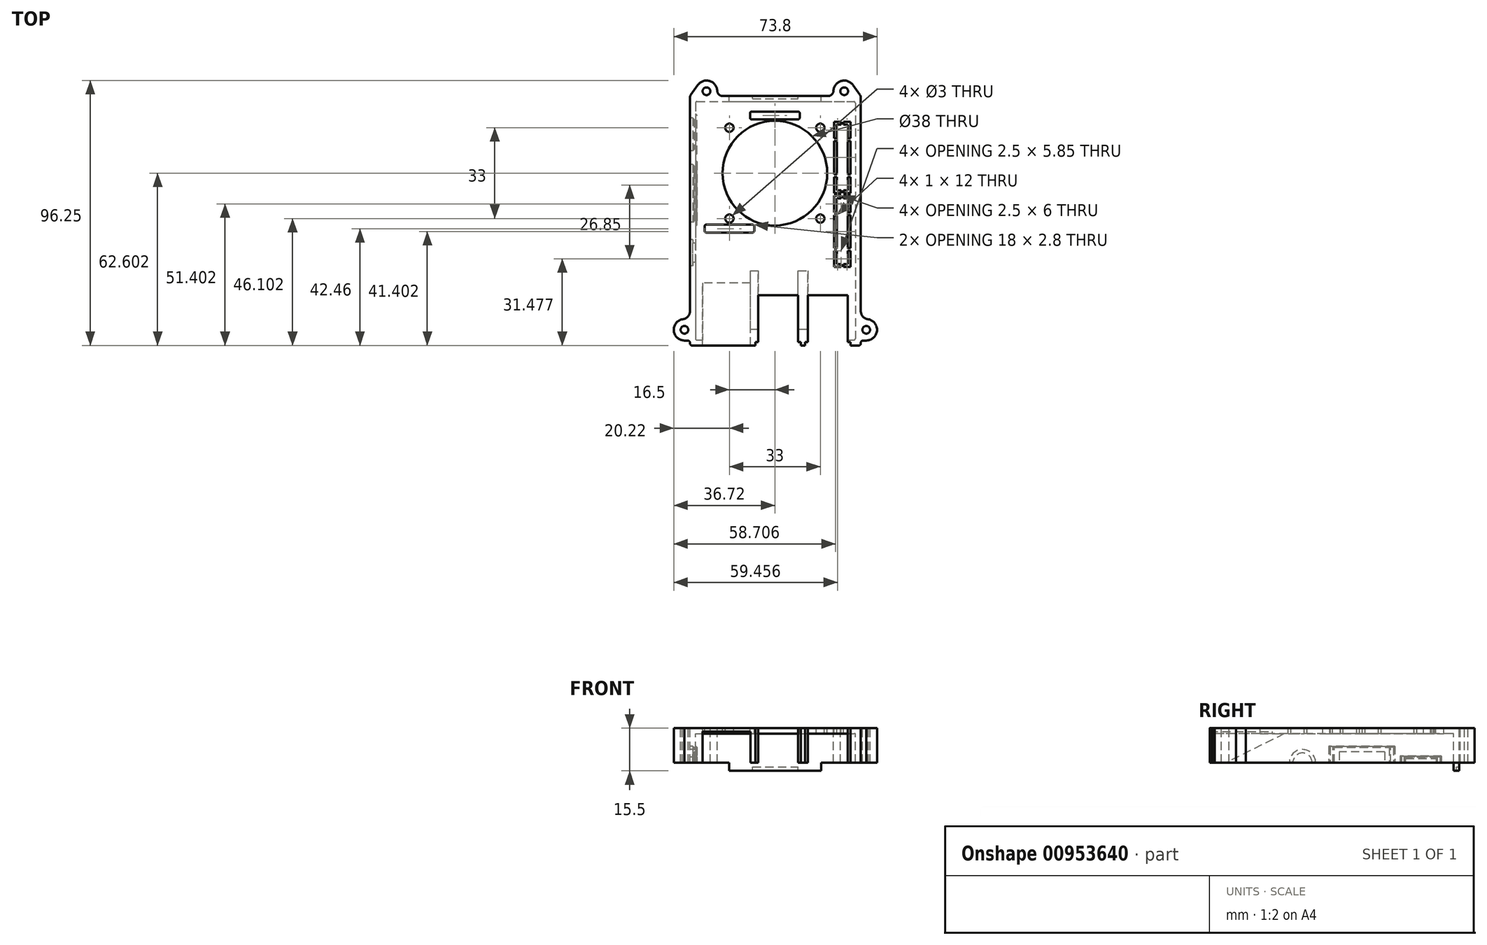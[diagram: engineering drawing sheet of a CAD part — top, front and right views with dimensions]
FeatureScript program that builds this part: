
annotation { "Feature Type Name" : "Feature", "Feature Type Description" : "" }
export const myFeature = defineFeature(function(context is Context, id is Id, definition is map)
    precondition{}
    {
        {
            var Q0;
            Q0=qCreatedBy(makeId("Top.planeOp"),FACE);
            var sketch = newSketch(context, id + "F0", { "sketchPlane" : qUnion([Q0])});
            skLineSegment(sketch, "E0.bottom", {"start": v(-18.95, 42.44) * mm, "end": v(19.3, 42.44) * mm});
            skLineSegment(sketch, "E0.top", {"start": v(-30.81, -48.16) * mm, "end": v(31.19, -48.16) * mm});
            skLineSegment(sketch, "E0.left", {"start": v(-30.81, 42.44) * mm, "end": v(-30.81, -35.67) * mm});
            skLineSegment(sketch, "E0.right", {"start": v(31.19, 42.44) * mm, "end": v(31.19, -35.68) * mm});
            skLineSegment(sketch, "E1.0", {"start": v(-28.31, -46.16) * mm, "end": v(28.69, -46.16) * mm});
            skLineSegment(sketch, "E1.1", {"start": v(29.19, 39.94) * mm, "end": v(29.19, -45.66) * mm});
            skLineSegment(sketch, "E1.2", {"start": v(-28.31, 40.44) * mm, "end": v(28.69, 40.44) * mm});
            skLineSegment(sketch, "E2.0", {"start": v(-28.81, 39.94) * mm, "end": v(-28.81, -45.66) * mm});
            skPoint(sketch, "E3.visualSharp", {"position": v(-28.81, 40.44) * mm});
            skArc(sketch, "E3.filletArc", {"start": v(-28.31, 40.44) * mm, "mid": v(-28.67, 40.3) * mm, "end": v(-28.81, 39.94) * mm});
            skPoint(sketch, "E4.visualSharp", {"position": v(29.19, 40.44) * mm});
            skArc(sketch, "E4.filletArc", {"start": v(29.19, 39.94) * mm, "mid": v(29.04, 40.3) * mm, "end": v(28.69, 40.44) * mm});
            skPoint(sketch, "E5.visualSharp", {"position": v(-28.81, -46.16) * mm});
            skArc(sketch, "E5.filletArc", {"start": v(-28.81, -45.66) * mm, "mid": v(-28.67, -46.01) * mm, "end": v(-28.31, -46.16) * mm});
            skPoint(sketch, "E6.visualSharp", {"position": v(29.19, -46.16) * mm});
            skArc(sketch, "E6.filletArc", {"start": v(28.69, -46.16) * mm, "mid": v(29.04, -46.01) * mm, "end": v(29.19, -45.66) * mm});
            skCircle(sketch, "E7", {"center": v(-24.82, 44.19) * mm, "radius": 1.4 * mm});
            skArc(sketch, "E8", {"start": v(-20.92, 44.35) * mm, "mid": v(-23.72, 47.93) * mm, "end": v(-28, 46.43) * mm});
            skLineSegment(sketch, "E9", {"start": v(-30.81, 42.44) * mm, "end": v(-28, 46.43) * mm});
            skFitSpline(sketch, "E10", {"points": [v(-18.95, 42.44) * mm, v(-20.92, 44.35) * mm], "startDerivative": vector(-2.9, 0) * mm, "endDerivative": vector(-0.3, 3.45) * mm});
            skFitSpline(sketch, "E11.MirrorCS", {"points": [v(19.3, 42.44) * mm, v(21.27, 44.35) * mm], "startDerivative": vector(2.9, 0) * mm, "endDerivative": vector(0.3, 3.45) * mm});
            skArc(sketch, "E12.MirrorCS", {"start": v(21.27, 44.35) * mm, "mid": v(24.07, 47.93) * mm, "end": v(28.36, 46.43) * mm});
            skLineSegment(sketch, "E13.MirrorCS", {"start": v(31.19, 42.44) * mm, "end": v(28.36, 46.43) * mm});
            skCircle(sketch, "E14.MirrorC", {"center": v(25.17, 44.19) * mm, "radius": 1.4 * mm});
            skCircle(sketch, "E15", {"center": v(-32.82, -42.46) * mm, "radius": 1.4 * mm});
            skArc(sketch, "E16", {"start": v(-33.56, -38.63) * mm, "mid": v(-36.7, -42.84) * mm, "end": v(-32.8, -46.36) * mm});
            skFitSpline(sketch, "E17", {"points": [v(-30.81, -35) * mm, v(-33.56, -38.63) * mm], "startDerivative": vector(0.46, -7.1) * mm, "endDerivative": vector(-4.36, -0.55) * mm});
            skFitSpline(sketch, "E18", {"points": [v(-30.81, -47.43) * mm, v(-32.8, -46.36) * mm], "startDerivative": vector(-0.12, 3.4) * mm, "endDerivative": vector(-4.35, -0.1) * mm});
            skLineSegment(sketch, "E19.trimOffspring", {"start": v(-30.81, -47.43) * mm, "end": v(-30.81, -48.16) * mm});
            skCircle(sketch, "E20.MirrorC", {"center": v(33.18, -42.46) * mm, "radius": 1.4 * mm});
            skFitSpline(sketch, "E21.MirrorCS", {"points": [v(31.17, -47.43) * mm, v(33.15, -46.36) * mm], "startDerivative": vector(0.12, 3.4) * mm, "endDerivative": vector(4.35, -0.1) * mm});
            skArc(sketch, "E22.MirrorCS", {"start": v(33.91, -38.63) * mm, "mid": v(37.06, -42.84) * mm, "end": v(33.15, -46.36) * mm});
            skFitSpline(sketch, "E23.MirrorCS", {"points": [v(31.19, -35) * mm, v(33.91, -38.63) * mm], "startDerivative": vector(-0.46, -7.1) * mm, "endDerivative": vector(4.36, -0.55) * mm});
            skLineSegment(sketch, "E24.trimOffspring", {"start": v(31.19, -47.17) * mm, "end": v(31.19, -48.16) * mm});
            skSolve(sketch);
        }
        {
            var Q0;
            Q0=makeQuery(id+"F0.imprint","IMPRINT",FACE,{"disambiguationData":[TD([[makeQuery(id+"F0.imprint","IMPRINT",EDGE,{"derivedFrom":sQuery(id+"F0.wireOp",EDGE,"E1.0")}),1.0]])]});
            var Q1;
            Q1=makeQuery(id+"F0.imprint","IMPRINT",FACE,{"disambiguationData":[TD([[makeQuery(id+"F0.imprint","IMPRINT",EDGE,{"derivedFrom":sQuery(id+"F0.wireOp",EDGE,"E0.top")}),1.0]])]});
            var Q2;
            {var subQ0=sQuery(id+"F0.wireOp",EDGE,"E11.MirrorCS");Q2=makeQuery(id+"F0.imprint","IMPRINT",FACE,{"disambiguationData":[TD([[makeQuery(id+"F0.imprint","IMPRINT",EDGE,{"derivedFrom":subQ0}),-1.0]])]});}
            extrude(context, id + "F1", {"entities" : qUnion([Q0, Q1, Q2]), "oppositeDirection" : true, "depth" : 2 * mm, "offsetDistance" : 25 * mm});
        }
        {
            var Q0;
            Q0=makeQuery(id+"F0.imprint","IMPRINT",FACE,{"disambiguationData":[TD([[makeQuery(id+"F0.imprint","IMPRINT",EDGE,{"derivedFrom":sQuery(id+"F0.wireOp",EDGE,"E0.bottom")}),-1.0]])]});
            extrude(context, id + "F2", {"entities" : qUnion([Q0]), "operationType" : NewBodyOperationType.ADD, "oppositeDirection" : true, "depth" : 12.5 * mm, "offsetDistance" : 25 * mm});
        }
        {
            var Q0;
            {var subQ0=sQuery(id+"F0.wireOp",EDGE,"E9");var subQ1=sQuery(id+"F0.wireOp",EDGE,"E0.left");Q0=makeQuery(id+"F2.boolean.opBoolean","MERGE",EDGE,{"derivedFrom":[makeQuery(id+"F1.opExtrude","SWEPT_EDGE",EDGE,{"disambiguationData":[OSD([subQ1,subQ0])]}),makeQuery(id+"F2.opExtrude","SWEPT_EDGE",EDGE,{"disambiguationData":[OSD([subQ1,subQ0])]})]});}
            var Q1;
            {var subQ0=sQuery(id+"F0.wireOp",EDGE,"E13.MirrorCS");var subQ1=sQuery(id+"F0.wireOp",EDGE,"E0.right");Q1=makeQuery(id+"F2.boolean.opBoolean","MERGE",EDGE,{"derivedFrom":[makeQuery(id+"F1.opExtrude","SWEPT_EDGE",EDGE,{"disambiguationData":[OSD([subQ1,subQ0])]}),makeQuery(id+"F2.opExtrude","SWEPT_EDGE",EDGE,{"disambiguationData":[OSD([subQ1,subQ0])]})]});}
            fillet(context, id + "F3", {"entities" : qUnion([Q0, Q1]), "radius" : 1.5 * mm, "tangentPropagation" : true, "allowEdgeOverflow" : false});
        }
        {
            var Q0;
            {var subQ0=sQuery(id+"F0.wireOp",EDGE,"E19.trimOffspring");var subQ1=sQuery(id+"F0.wireOp",EDGE,"E0.top");Q0=makeQuery(id+"F2.boolean.opBoolean","MERGE",EDGE,{"derivedFrom":[makeQuery(id+"F1.opExtrude","SWEPT_EDGE",EDGE,{"disambiguationData":[OSD([subQ1,subQ0])]}),makeQuery(id+"F2.opExtrude","SWEPT_EDGE",EDGE,{"disambiguationData":[OSD([subQ1,subQ0])]})]});}
            var Q1;
            {var subQ0=sQuery(id+"F0.wireOp",EDGE,"E24.trimOffspring");var subQ1=sQuery(id+"F0.wireOp",EDGE,"E0.top");Q1=makeQuery(id+"F2.boolean.opBoolean","MERGE",EDGE,{"derivedFrom":[makeQuery(id+"F1.opExtrude","SWEPT_EDGE",EDGE,{"disambiguationData":[OSD([subQ1,subQ0])]}),makeQuery(id+"F2.opExtrude","SWEPT_EDGE",EDGE,{"disambiguationData":[OSD([subQ1,subQ0])]})]});}
            fillet(context, id + "F4", {"entities" : qUnion([Q0, Q1]), "radius" : 0.77 * mm, "tangentPropagation" : true, "allowEdgeOverflow" : false});
        }
        {
            var Q0;
            Q0=makeQuery(id+"F1.opExtrude","CAP_FACE",FACE,{"disambiguationData":[OSD([sQuery(id+"F0.wireOp",EDGE,"E0.bottom"),sQuery(id+"F0.wireOp",EDGE,"E0.top"),sQuery(id+"F0.wireOp",EDGE,"E0.left"),sQuery(id+"F0.wireOp",EDGE,"E0.right"),sQuery(id+"F0.wireOp",EDGE,"E7"),sQuery(id+"F0.wireOp",EDGE,"E8"),sQuery(id+"F0.wireOp",EDGE,"E9"),sQuery(id+"F0.wireOp",EDGE,"E10"),sQuery(id+"F0.wireOp",EDGE,"E11.MirrorCS"),sQuery(id+"F0.wireOp",EDGE,"E12.MirrorCS"),sQuery(id+"F0.wireOp",EDGE,"E13.MirrorCS"),sQuery(id+"F0.wireOp",EDGE,"E14.MirrorC"),sQuery(id+"F0.wireOp",EDGE,"E15"),sQuery(id+"F0.wireOp",EDGE,"E16"),sQuery(id+"F0.wireOp",EDGE,"E17"),sQuery(id+"F0.wireOp",EDGE,"E18"),sQuery(id+"F0.wireOp",EDGE,"E19.trimOffspring"),sQuery(id+"F0.wireOp",EDGE,"E20.MirrorC"),sQuery(id+"F0.wireOp",EDGE,"E21.MirrorCS"),sQuery(id+"F0.wireOp",EDGE,"E22.MirrorCS"),sQuery(id+"F0.wireOp",EDGE,"E23.MirrorCS"),sQuery(id+"F0.wireOp",EDGE,"E24.trimOffspring")])],"isStart":false});
            var sketch = newSketch(context, id + "F5", { "sketchPlane" : qUnion([Q0])});
            skLineSegment(sketch, "E25.bottom", {"start": v(-8.87, 48.16) * mm, "end": v(-6.07, 48.16) * mm});
            skLineSegment(sketch, "E25.top", {"start": v(-8.87, 21.06) * mm, "end": v(-6.07, 21.06) * mm});
            skLineSegment(sketch, "E25.left", {"start": v(-8.87, 48.16) * mm, "end": v(-8.87, 21.06) * mm});
            skLineSegment(sketch, "E25.right", {"start": v(-6.07, 48.16) * mm, "end": v(-6.07, 21.06) * mm});
            skLineSegment(sketch, "E26.bottom", {"start": v(8.43, 48.16) * mm, "end": v(11.93, 48.16) * mm});
            skLineSegment(sketch, "E26.top", {"start": v(8.43, 21.06) * mm, "end": v(11.93, 21.06) * mm});
            skLineSegment(sketch, "E26.left", {"start": v(8.43, 48.16) * mm, "end": v(8.43, 21.06) * mm});
            skLineSegment(sketch, "E26.right", {"start": v(11.93, 48.16) * mm, "end": v(11.93, 21.06) * mm});
            skSolve(sketch);
        }
        {
            var Q0;
            Q0 = qSketchRegion(id + "F5", true);
            extrude(context, id + "F6", {"entities" : qUnion([Q0]), "operationType" : NewBodyOperationType.ADD, "depth" : 10.5 * mm, "offsetDistance" : 25 * mm});
        }
        {
            var Q0;
            Q0=makeQuery(id+"F6.opExtrude","CAP_EDGE",EDGE,{"disambiguationData":[OSD([sQuery(id+"F5.wireOp",EDGE,"E25.top")])],"isStart":false});
            var Q1;
            Q1=makeQuery(id+"F6.opExtrude","CAP_EDGE",EDGE,{"disambiguationData":[OSD([sQuery(id+"F5.wireOp",EDGE,"E26.top")])],"isStart":false});
            chamfer(context, id + "F7", {"entities" : qUnion([Q0, Q1]), "chamferType" : ChamferType.TWO_OFFSETS, "width1" : 21.1 * mm, "oppositeDirection" : false, "width2" : 10.5 * mm, "tangentPropagation" : true});
        }
        {
            var Q0;
            Q0=makeQuery(id+"F0.imprint","IMPRINT",FACE,{"disambiguationData":[TD([[makeQuery(id+"F0.imprint","IMPRINT",EDGE,{"derivedFrom":sQuery(id+"F0.wireOp",EDGE,"E1.0")}),1.0]])]});
            var sketch = newSketch(context, id + "F8", { "sketchPlane" : qUnion([Q0])});
            skLineSegment(sketch, "E27.bottom", {"start": v(-6.07, -29.86) * mm, "end": v(8.43, -29.86) * mm});
            skLineSegment(sketch, "E27.top", {"start": v(-6.07, -48.16) * mm, "end": v(8.43, -48.16) * mm});
            skLineSegment(sketch, "E27.left", {"start": v(-6.07, -29.86) * mm, "end": v(-6.07, -46.93) * mm});
            skLineSegment(sketch, "E27.right", {"start": v(8.43, -29.86) * mm, "end": v(8.43, -46.93) * mm});
            skLineSegment(sketch, "E28.bottom", {"start": v(11.93, -29.86) * mm, "end": v(26.43, -29.86) * mm});
            skLineSegment(sketch, "E28.top", {"start": v(11.93, -48.16) * mm, "end": v(26.43, -48.16) * mm});
            skLineSegment(sketch, "E28.left", {"start": v(11.93, -29.86) * mm, "end": v(11.93, -46.93) * mm});
            skLineSegment(sketch, "E28.right", {"start": v(26.43, -29.86) * mm, "end": v(26.43, -46.93) * mm});
            skLineSegment(sketch, "E29.bottom", {"start": v(-6.07, -48.16) * mm, "end": v(-7.07, -48.16) * mm});
            skLineSegment(sketch, "E29.top", {"start": v(-6.07, -46.93) * mm, "end": v(-7.07, -46.93) * mm});
            skLineSegment(sketch, "E29.right", {"start": v(-7.07, -48.16) * mm, "end": v(-7.07, -46.93) * mm});
            skLineSegment(sketch, "E30.bottom", {"start": v(8.43, -48.16) * mm, "end": v(9.43, -48.16) * mm});
            skLineSegment(sketch, "E30.top", {"start": v(8.43, -46.93) * mm, "end": v(9.43, -46.93) * mm});
            skLineSegment(sketch, "E30.right", {"start": v(9.43, -48.16) * mm, "end": v(9.43, -46.93) * mm});
            skLineSegment(sketch, "E31.bottom", {"start": v(11.93, -48.16) * mm, "end": v(10.93, -48.16) * mm});
            skLineSegment(sketch, "E31.top", {"start": v(11.93, -46.93) * mm, "end": v(10.93, -46.93) * mm});
            skLineSegment(sketch, "E31.right", {"start": v(10.93, -48.16) * mm, "end": v(10.93, -46.93) * mm});
            skLineSegment(sketch, "E32.bottom", {"start": v(26.43, -48.16) * mm, "end": v(27.43, -48.16) * mm});
            skLineSegment(sketch, "E32.top", {"start": v(26.43, -46.93) * mm, "end": v(27.43, -46.93) * mm});
            skLineSegment(sketch, "E32.right", {"start": v(27.43, -48.16) * mm, "end": v(27.43, -46.93) * mm});
            skSolve(sketch);
        }
        {
            var Q0;
            Q0=makeQuery(id+"F8.imprint","IMPRINT",FACE,{"disambiguationData":[TD([[makeQuery(id+"F8.imprint","IMPRINT",EDGE,{"derivedFrom":sQuery(id+"F8.wireOp",EDGE,"E27.top")}),1.0]])]});
            var Q1;
            {var subQ0=sQuery(id+"F8.wireOp",EDGE,"E27.bottom");Q1=makeQuery(id+"F8.imprint","IMPRINT",FACE,{"disambiguationData":[TD([[makeQuery(id+"F8.imprint","IMPRINT",EDGE,{"derivedFrom":subQ0}),-1.0]])]});}
            var Q2;
            Q2=makeQuery(id+"F8.imprint","IMPRINT",FACE,{"disambiguationData":[TD([[makeQuery(id+"F8.imprint","IMPRINT",EDGE,{"derivedFrom":sQuery(id+"F8.wireOp",EDGE,"E28.top")}),1.0]])]});
            var Q3;
            {var subQ0=sQuery(id+"F8.wireOp",EDGE,"E28.bottom");Q3=makeQuery(id+"F8.imprint","IMPRINT",FACE,{"disambiguationData":[TD([[makeQuery(id+"F8.imprint","IMPRINT",EDGE,{"derivedFrom":subQ0}),-1.0]])]});}
            var Q4;
            Q4=makeQuery(id+"F6.boolean.opBoolean","MERGE",FACE,{"derivedFrom":[makeQuery(id+"F2.opExtrude","CAP_FACE",FACE,{"disambiguationData":[OSD([sQuery(id+"F0.wireOp",EDGE,"E0.bottom"),sQuery(id+"F0.wireOp",EDGE,"E0.top"),sQuery(id+"F0.wireOp",EDGE,"E0.left"),sQuery(id+"F0.wireOp",EDGE,"E0.right"),sQuery(id+"F0.wireOp",EDGE,"E1.0"),sQuery(id+"F0.wireOp",EDGE,"E1.1"),sQuery(id+"F0.wireOp",EDGE,"E1.2"),sQuery(id+"F0.wireOp",EDGE,"E2.0"),sQuery(id+"F0.wireOp",EDGE,"E3.filletArc"),sQuery(id+"F0.wireOp",EDGE,"E4.filletArc"),sQuery(id+"F0.wireOp",EDGE,"E5.filletArc"),sQuery(id+"F0.wireOp",EDGE,"E6.filletArc"),sQuery(id+"F0.wireOp",EDGE,"E7"),sQuery(id+"F0.wireOp",EDGE,"E8"),sQuery(id+"F0.wireOp",EDGE,"E9"),sQuery(id+"F0.wireOp",EDGE,"E10"),sQuery(id+"F0.wireOp",EDGE,"E11.MirrorCS"),sQuery(id+"F0.wireOp",EDGE,"E12.MirrorCS"),sQuery(id+"F0.wireOp",EDGE,"E13.MirrorCS"),sQuery(id+"F0.wireOp",EDGE,"E14.MirrorC"),sQuery(id+"F0.wireOp",EDGE,"E15"),sQuery(id+"F0.wireOp",EDGE,"E16"),sQuery(id+"F0.wireOp",EDGE,"E17"),sQuery(id+"F0.wireOp",EDGE,"E18"),sQuery(id+"F0.wireOp",EDGE,"E19.trimOffspring"),sQuery(id+"F0.wireOp",EDGE,"E20.MirrorC"),sQuery(id+"F0.wireOp",EDGE,"E21.MirrorCS"),sQuery(id+"F0.wireOp",EDGE,"E22.MirrorCS"),sQuery(id+"F0.wireOp",EDGE,"E23.MirrorCS"),sQuery(id+"F0.wireOp",EDGE,"E24.trimOffspring")])],"isStart":false}),makeQuery(id+"F6.opExtrude","CAP_FACE",FACE,{"disambiguationData":[OSD([sQuery(id+"F5.wireOp",EDGE,"E25.bottom"),sQuery(id+"F5.wireOp",EDGE,"E25.top"),sQuery(id+"F5.wireOp",EDGE,"E25.left"),sQuery(id+"F5.wireOp",EDGE,"E25.right")])],"isStart":false}),makeQuery(id+"F6.opExtrude","CAP_FACE",FACE,{"disambiguationData":[OSD([sQuery(id+"F5.wireOp",EDGE,"E26.bottom"),sQuery(id+"F5.wireOp",EDGE,"E26.top"),sQuery(id+"F5.wireOp",EDGE,"E26.left"),sQuery(id+"F5.wireOp",EDGE,"E26.right")])],"isStart":false})]});
            extrude(context, id + "F9", {"entities" : qUnion([Q0, Q1, Q2, Q3]), "operationType" : NewBodyOperationType.REMOVE, "endBound" : BoundingType.UP_TO_SURFACE, "oppositeDirection" : true, "depth" : 10.5 * mm, "endBoundEntityFace" : qUnion([Q4]), "offsetDistance" : 25 * mm});
        }
        {
            var Q0;
            Q0=makeQuery(id+"F1.opExtrude","CAP_FACE",FACE,{"disambiguationData":[OSD([sQuery(id+"F0.wireOp",EDGE,"E0.bottom"),sQuery(id+"F0.wireOp",EDGE,"E0.top"),sQuery(id+"F0.wireOp",EDGE,"E0.left"),sQuery(id+"F0.wireOp",EDGE,"E0.right"),sQuery(id+"F0.wireOp",EDGE,"E7"),sQuery(id+"F0.wireOp",EDGE,"E8"),sQuery(id+"F0.wireOp",EDGE,"E9"),sQuery(id+"F0.wireOp",EDGE,"E10"),sQuery(id+"F0.wireOp",EDGE,"E11.MirrorCS"),sQuery(id+"F0.wireOp",EDGE,"E12.MirrorCS"),sQuery(id+"F0.wireOp",EDGE,"E13.MirrorCS"),sQuery(id+"F0.wireOp",EDGE,"E14.MirrorC"),sQuery(id+"F0.wireOp",EDGE,"E15"),sQuery(id+"F0.wireOp",EDGE,"E16"),sQuery(id+"F0.wireOp",EDGE,"E17"),sQuery(id+"F0.wireOp",EDGE,"E18"),sQuery(id+"F0.wireOp",EDGE,"E19.trimOffspring"),sQuery(id+"F0.wireOp",EDGE,"E20.MirrorC"),sQuery(id+"F0.wireOp",EDGE,"E21.MirrorCS"),sQuery(id+"F0.wireOp",EDGE,"E22.MirrorCS"),sQuery(id+"F0.wireOp",EDGE,"E23.MirrorCS"),sQuery(id+"F0.wireOp",EDGE,"E24.trimOffspring")])],"isStart":false});
            var sketch = newSketch(context, id + "F10", { "sketchPlane" : qUnion([Q0])});
            skLineSegment(sketch, "E33.bottom", {"start": v(-26.27, 48.16) * mm, "end": v(-8.87, 48.16) * mm});
            skLineSegment(sketch, "E33.top", {"start": v(-26.27, 25.46) * mm, "end": v(-8.87, 25.46) * mm});
            skLineSegment(sketch, "E33.left", {"start": v(-26.27, 48.16) * mm, "end": v(-26.27, 25.46) * mm});
            skLineSegment(sketch, "E33.right", {"start": v(-8.87, 48.16) * mm, "end": v(-8.87, 25.46) * mm});
            skSolve(sketch);
        }
        {
            var Q0;
            {var subQ0=sQuery(id+"F10.wireOp",EDGE,"E33.bottom");Q0=makeQuery(id+"F10.imprint","IMPRINT",FACE,{"disambiguationData":[TD([[makeQuery(id+"F10.imprint","IMPRINT",EDGE,{"derivedFrom":subQ0}),-1.0]])]});}
            var Q1;
            {var subQ0=sQuery(id+"F10.wireOp",EDGE,"E33.top");Q1=makeQuery(id+"F10.imprint","IMPRINT",FACE,{"disambiguationData":[TD([[makeQuery(id+"F10.imprint","IMPRINT",EDGE,{"derivedFrom":subQ0}),1.0]])]});}
            var Q2;
            {var subQ0=sQuery(id+"F0.wireOp",EDGE,"E17");var subQ1=sQuery(id+"F0.wireOp",EDGE,"E16");var subQ2=sQuery(id+"F0.wireOp",EDGE,"E14.MirrorC");var subQ3=sQuery(id+"F0.wireOp",EDGE,"E13.MirrorCS");var subQ4=sQuery(id+"F0.wireOp",EDGE,"E12.MirrorCS");var subQ5=sQuery(id+"F0.wireOp",EDGE,"E11.MirrorCS");var subQ6=sQuery(id+"F0.wireOp",EDGE,"E10");var subQ7=sQuery(id+"F0.wireOp",EDGE,"E24.trimOffspring");var subQ8=sQuery(id+"F0.wireOp",EDGE,"E9");var subQ9=sQuery(id+"F0.wireOp",EDGE,"E23.MirrorCS");var subQ10=sQuery(id+"F0.wireOp",EDGE,"E8");var subQ11=sQuery(id+"F0.wireOp",EDGE,"E22.MirrorCS");var subQ12=sQuery(id+"F0.wireOp",EDGE,"E7");var subQ13=sQuery(id+"F0.wireOp",EDGE,"E21.MirrorCS");var subQ14=sQuery(id+"F0.wireOp",EDGE,"E6.filletArc");var subQ15=sQuery(id+"F0.wireOp",EDGE,"E20.MirrorC");var subQ16=sQuery(id+"F0.wireOp",EDGE,"E5.filletArc");var subQ17=sQuery(id+"F0.wireOp",EDGE,"E19.trimOffspring");var subQ18=sQuery(id+"F0.wireOp",EDGE,"E4.filletArc");var subQ19=sQuery(id+"F0.wireOp",EDGE,"E18");var subQ20=sQuery(id+"F0.wireOp",EDGE,"E3.filletArc");var subQ21=sQuery(id+"F0.wireOp",EDGE,"E2.0");var subQ22=sQuery(id+"F0.wireOp",EDGE,"E1.2");var subQ23=sQuery(id+"F0.wireOp",EDGE,"E15");var subQ24=sQuery(id+"F0.wireOp",EDGE,"E1.1");var subQ25=sQuery(id+"F0.wireOp",EDGE,"E1.0");var subQ26=sQuery(id+"F0.wireOp",EDGE,"E0.right");var subQ27=sQuery(id+"F0.wireOp",EDGE,"E0.left");var subQ28=sQuery(id+"F0.wireOp",EDGE,"E0.top");var subQ29=sQuery(id+"F0.wireOp",EDGE,"E0.bottom");var subQ30=sQuery(id+"F5.wireOp",EDGE,"E25.left");var subQ31=sQuery(id+"F5.wireOp",EDGE,"E25.right");var subQ32=sQuery(id+"F5.wireOp",EDGE,"E25.top");Q2=makeQuery(id+"F9.boolean.opBoolean","SPLIT",FACE,{"disambiguationData":[TD([makeQuery(id+"F1.opExtrude","SWEPT_FACE",FACE,{"disambiguationData":[OSD([subQ29])]})])],"derivedFrom":makeQuery(id+"F6.boolean.opBoolean","MERGE",FACE,{"derivedFrom":[makeQuery(id+"F2.opExtrude","CAP_FACE",FACE,{"disambiguationData":[OSD([subQ29,subQ28,subQ27,subQ26,subQ25,subQ24,subQ22,subQ21,subQ20,subQ18,subQ16,subQ14,subQ12,subQ10,subQ8,subQ6,subQ5,subQ4,subQ3,subQ2,subQ23,subQ1,subQ0,subQ19,subQ17,subQ15,subQ13,subQ11,subQ9,subQ7])],"isStart":false}),makeQuery(id+"F6.opExtrude","CAP_FACE",FACE,{"disambiguationData":[OSD([sQuery(id+"F5.wireOp",EDGE,"E25.bottom"),subQ32,subQ30,subQ31])],"isStart":false}),makeQuery(id+"F6.opExtrude","CAP_FACE",FACE,{"disambiguationData":[OSD([sQuery(id+"F5.wireOp",EDGE,"E26.bottom"),sQuery(id+"F5.wireOp",EDGE,"E26.top"),sQuery(id+"F5.wireOp",EDGE,"E26.left"),sQuery(id+"F5.wireOp",EDGE,"E26.right")])],"isStart":false})]})});}
            extrude(context, id + "F11", {"entities" : qUnion([Q0, Q1]), "operationType" : NewBodyOperationType.REMOVE, "oppositeDirection" : true, "depth" : 0.8 * mm, "offsetDistance" : 25 * mm, "hasSecondDirection" : true, "secondDirectionBound" : SecondDirectionBoundingType.UP_TO_SURFACE, "secondDirectionOppositeDirection" : false, "secondDirectionDepth" : 25 * mm, "secondDirectionBoundEntityFace" : qUnion([Q2])});
        }
        {
            var Q0;
            {var subQ0=sQuery(id+"F0.wireOp",EDGE,"E0.left");Q0=makeQuery(id+"F2.boolean.opBoolean","MERGE",FACE,{"derivedFrom":[makeQuery(id+"F1.opExtrude","SWEPT_FACE",FACE,{"disambiguationData":[OSD([subQ0])]}),makeQuery(id+"F2.opExtrude","SWEPT_FACE",FACE,{"disambiguationData":[OSD([subQ0])]})]});}
            var sketch = newSketch(context, id + "F12", { "sketchPlane" : qUnion([Q0])});
            skArc(sketch, "E34", {"start": v(19.2, -12.5) * mm, "mid": v(14.46, -7.76) * mm, "end": v(9.71, -12.5) * mm});
            skSolve(sketch);
        }
        {
            var Q0;
            {var subQ0=sQuery(id+"F12.wireOp",EDGE,"E34");Q0=makeQuery(id+"F12.imprint","IMPRINT",FACE,{"disambiguationData":[TD([[makeQuery(id+"F12.imprint","IMPRINT",EDGE,{"derivedFrom":subQ0}),1.0]])]});}
            extrude(context, id + "F13", {"entities" : qUnion([Q0]), "operationType" : NewBodyOperationType.REMOVE, "oppositeDirection" : true, "depth" : 1 * mm, "offsetDistance" : 25 * mm});
        }
        {
            var Q0;
            Q0=makeQuery(id+"F13.boolean.opBoolean","COPY",FACE,{"derivedFrom":makeQuery(id+"F13.opExtrude","CAP_FACE",FACE,{"disambiguationData":[OSD([sQuery(id+"F0.wireOp",EDGE,"E0.left"),sQuery(id+"F12.wireOp",EDGE,"E34")])],"isStart":false})});
            var sketch = newSketch(context, id + "F14", { "sketchPlane" : qUnion([Q0])});
            skArc(sketch, "E35", {"start": v(17.96, -12.5) * mm, "mid": v(14.46, -9) * mm, "end": v(10.96, -12.5) * mm});
            skSolve(sketch);
        }
        {
            var Q0;
            {var subQ0=sQuery(id+"F14.wireOp",EDGE,"E35");Q0=makeQuery(id+"F14.imprint","IMPRINT",FACE,{"disambiguationData":[TD([[makeQuery(id+"F14.imprint","IMPRINT",EDGE,{"derivedFrom":subQ0}),1.0]])]});}
            var Q1;
            Q1=makeQuery(id+"F2.opExtrude","SWEPT_FACE",FACE,{"disambiguationData":[OSD([sQuery(id+"F0.wireOp",EDGE,"E2.0")])]});
            extrude(context, id + "F15", {"entities" : qUnion([Q0]), "operationType" : NewBodyOperationType.REMOVE, "endBound" : BoundingType.UP_TO_SURFACE, "oppositeDirection" : true, "depth" : 25 * mm, "endBoundEntityFace" : qUnion([Q1]), "offsetDistance" : 25 * mm});
        }
        {
            var Q0;
            {var subQ5=sQuery(id+"F12.wireOp",EDGE,"E34");Q0=makeQuery(id+"F12.imprint","IMPRINT",FACE,{"disambiguationData":[TD([[makeQuery(id+"F12.imprint","IMPRINT",EDGE,{"derivedFrom":subQ5}),-1.0]])]});}
            var sketch = newSketch(context, id + "F16", { "sketchPlane" : qUnion([Q0])});
            skLineSegment(sketch, "E36.bottom", {"start": v(3.41, -12.5) * mm, "end": v(-17.59, -12.5) * mm});
            skLineSegment(sketch, "E36.top", {"start": v(3.41, -6.5) * mm, "end": v(-17.59, -6.5) * mm});
            skLineSegment(sketch, "E36.left", {"start": v(3.41, -12.5) * mm, "end": v(3.41, -6.5) * mm});
            skLineSegment(sketch, "E36.right", {"start": v(-17.59, -12.5) * mm, "end": v(-17.59, -6.5) * mm});
            skSolve(sketch);
        }
        {
            var Q0;
            Q0=makeQuery(id+"F16.imprint","IMPRINT",FACE,{"disambiguationData":[TD([[makeQuery(id+"F16.imprint","IMPRINT",EDGE,{"derivedFrom":sQuery(id+"F16.wireOp",EDGE,"E36.bottom")}),1.0]])]});
            extrude(context, id + "F17", {"entities" : qUnion([Q0]), "operationType" : NewBodyOperationType.REMOVE, "oppositeDirection" : true, "depth" : 1.5 * mm, "offsetDistance" : 25 * mm});
        }
        {
            var Q0;
            {var subQ2=sQuery(id+"F0.wireOp",EDGE,"E14.MirrorC");var subQ4=sQuery(id+"F0.wireOp",EDGE,"E13.MirrorCS");var subQ6=sQuery(id+"F0.wireOp",EDGE,"E12.MirrorCS");var subQ8=sQuery(id+"F0.wireOp",EDGE,"E24.trimOffspring");var subQ9=sQuery(id+"F0.wireOp",EDGE,"E0.top");var subQ11=sQuery(id+"F0.wireOp",EDGE,"E11.MirrorCS");var subQ13=sQuery(id+"F0.wireOp",EDGE,"E10");var subQ16=sQuery(id+"F0.wireOp",EDGE,"E9");var subQ18=sQuery(id+"F0.wireOp",EDGE,"E23.MirrorCS");var subQ20=sQuery(id+"F0.wireOp",EDGE,"E8");var subQ22=sQuery(id+"F0.wireOp",EDGE,"E22.MirrorCS");var subQ24=sQuery(id+"F0.wireOp",EDGE,"E7");var subQ26=sQuery(id+"F0.wireOp",EDGE,"E21.MirrorCS");var subQ28=sQuery(id+"F0.wireOp",EDGE,"E6.filletArc");var subQ30=sQuery(id+"F0.wireOp",EDGE,"E0.right");var subQ32=sQuery(id+"F0.wireOp",EDGE,"E20.MirrorC");var subQ34=sQuery(id+"F0.wireOp",EDGE,"E4.filletArc");var subQ36=sQuery(id+"F0.wireOp",EDGE,"E3.filletArc");var subQ38=sQuery(id+"F0.wireOp",EDGE,"E2.0");var subQ40=sQuery(id+"F0.wireOp",EDGE,"E1.2");var subQ42=sQuery(id+"F0.wireOp",EDGE,"E1.1");var subQ46=sQuery(id+"F0.wireOp",EDGE,"E0.left");var subQ51=sQuery(id+"F0.wireOp",EDGE,"E0.bottom");var subQ63=makeQuery(id+"F1.opExtrude","SWEPT_FACE",FACE,{"disambiguationData":[OSD([subQ51])]});var subQ69=sQuery(id+"F0.wireOp",EDGE,"E1.0");var subQ75=sQuery(id+"F0.wireOp",EDGE,"E17");var subQ77=sQuery(id+"F0.wireOp",EDGE,"E16");var subQ79=sQuery(id+"F0.wireOp",EDGE,"E19.trimOffspring");var subQ81=sQuery(id+"F0.wireOp",EDGE,"E5.filletArc");var subQ83=sQuery(id+"F0.wireOp",EDGE,"E18");var subQ87=sQuery(id+"F0.wireOp",EDGE,"E15");var subQ91=sQuery(id+"F5.wireOp",EDGE,"E25.left");var subQ92=sQuery(id+"F5.wireOp",EDGE,"E25.right");var subQ93=sQuery(id+"F5.wireOp",EDGE,"E25.top");Q0=makeQuery(id+"F15.boolean.opBoolean","SPLIT",FACE,{"disambiguationData":[TD([subQ63])],"derivedFrom":makeQuery(id+"F11.boolean.opBoolean","SPLIT",FACE,{"disambiguationData":[TD([subQ63])],"derivedFrom":makeQuery(id+"F9.boolean.opBoolean","SPLIT",FACE,{"disambiguationData":[TD([subQ63])],"derivedFrom":makeQuery(id+"F6.boolean.opBoolean","MERGE",FACE,{"derivedFrom":[makeQuery(id+"F2.opExtrude","CAP_FACE",FACE,{"disambiguationData":[OSD([subQ51,subQ9,subQ46,subQ30,subQ69,subQ42,subQ40,subQ38,subQ36,subQ34,subQ81,subQ28,subQ24,subQ20,subQ16,subQ13,subQ11,subQ6,subQ4,subQ2,subQ87,subQ77,subQ75,subQ83,subQ79,subQ32,subQ26,subQ22,subQ18,subQ8])],"isStart":false}),makeQuery(id+"F6.opExtrude","CAP_FACE",FACE,{"disambiguationData":[OSD([sQuery(id+"F5.wireOp",EDGE,"E25.bottom"),subQ93,subQ91,subQ92])],"isStart":false}),makeQuery(id+"F6.opExtrude","CAP_FACE",FACE,{"disambiguationData":[OSD([sQuery(id+"F5.wireOp",EDGE,"E26.bottom"),sQuery(id+"F5.wireOp",EDGE,"E26.top"),sQuery(id+"F5.wireOp",EDGE,"E26.left"),sQuery(id+"F5.wireOp",EDGE,"E26.right")])],"isStart":false})]})})})});}
            var sketch = newSketch(context, id + "F18", { "sketchPlane" : qUnion([Q0])});
            skLineSegment(sketch, "E37.left", {"start": v(-28.81, 4.9) * mm, "end": v(-28.81, -19.1) * mm});
            skLineSegment(sketch, "E37.right", {"start": v(-28.32, 4.4) * mm, "end": v(-28.32, -18.61) * mm});
            skLineSegment(sketch, "E38", {"start": v(-28.81, 4.9) * mm, "end": v(-28.32, 4.4) * mm});
            skLineSegment(sketch, "E39", {"start": v(-28.81, -19.1) * mm, "end": v(-28.32, -18.61) * mm});
            skLineSegment(sketch, "E40.left", {"start": v(-28.81, -21.01) * mm, "end": v(-28.81, -36.01) * mm});
            skLineSegment(sketch, "E40.right", {"start": v(-28.32, -21.5) * mm, "end": v(-28.32, -35.52) * mm});
            skLineSegment(sketch, "E41", {"start": v(-28.81, -21.01) * mm, "end": v(-28.32, -21.5) * mm});
            skLineSegment(sketch, "E42", {"start": v(-28.81, -36.01) * mm, "end": v(-28.32, -35.52) * mm});
            skSolve(sketch);
        }
        {
            var Q0;
            {var subQ0=sQuery(id+"F18.wireOp",EDGE,"E37.right");Q0=makeQuery(id+"F18.imprint","IMPRINT",FACE,{"disambiguationData":[TD([[makeQuery(id+"F18.imprint","IMPRINT",EDGE,{"derivedFrom":subQ0}),-1.0]])]});}
            extrude(context, id + "F19", {"entities" : qUnion([Q0]), "operationType" : NewBodyOperationType.ADD, "oppositeDirection" : true, "depth" : 6 * mm, "offsetDistance" : 25 * mm});
        }
        {
            var Q0;
            Q0 = qSketchRegion(id + "F18", true);
            extrude(context, id + "F20", {"entities" : qUnion([Q0]), "operationType" : NewBodyOperationType.ADD, "oppositeDirection" : true, "depth" : 2.4 * mm, "offsetDistance" : 25 * mm});
        }
        {
            var Q0;
            Q0=makeQuery(id+"F20.opExtrude","CAP_EDGE",EDGE,{"disambiguationData":[OSD([sQuery(id+"F18.wireOp",EDGE,"E40.right")])],"isStart":false});
            var Q1;
            Q1=makeQuery(id+"F19.opExtrude","CAP_EDGE",EDGE,{"disambiguationData":[OSD([sQuery(id+"F18.wireOp",EDGE,"E37.right")])],"isStart":false});
            chamfer(context, id + "F21", {"entities" : qUnion([Q0, Q1]), "width" : 0.4 * mm, "tangentPropagation" : true});
        }
        {
            var Q0;
            {var subQ5=sQuery(id+"F12.wireOp",EDGE,"E34");Q0=makeQuery(id+"F12.imprint","IMPRINT",FACE,{"disambiguationData":[TD([[makeQuery(id+"F12.imprint","IMPRINT",EDGE,{"derivedFrom":subQ5}),-1.0]])]});}
            var sketch = newSketch(context, id + "F22", { "sketchPlane" : qUnion([Q0])});
            skLineSegment(sketch, "E43.bottom", {"start": v(-22.52, -12.5) * mm, "end": v(-34.52, -12.5) * mm});
            skLineSegment(sketch, "E43.top", {"start": v(-22.52, -10.5) * mm, "end": v(-34.52, -10.5) * mm});
            skLineSegment(sketch, "E43.left", {"start": v(-22.52, -12.5) * mm, "end": v(-22.52, -10.5) * mm});
            skLineSegment(sketch, "E43.right", {"start": v(-34.52, -12.5) * mm, "end": v(-34.52, -10.5) * mm});
            skLineSegment(sketch, "E44.bottom", {"start": v(-15.37, -8.6) * mm, "end": v(1.13, -8.6) * mm});
            skLineSegment(sketch, "E44.top", {"start": v(-15.37, -12.5) * mm, "end": v(1.13, -12.5) * mm});
            skLineSegment(sketch, "E44.left", {"start": v(-15.37, -8.6) * mm, "end": v(-15.37, -12.5) * mm});
            skLineSegment(sketch, "E44.right", {"start": v(1.13, -8.6) * mm, "end": v(1.13, -12.5) * mm});
            skSolve(sketch);
        }
        {
            var Q0;
            Q0=makeQuery(id+"F22.imprint","IMPRINT",FACE,{"disambiguationData":[TD([[makeQuery(id+"F22.imprint","IMPRINT",EDGE,{"derivedFrom":sQuery(id+"F22.wireOp",EDGE,"E44.bottom")}),-1.0]])]});
            var Q1;
            Q1=makeQuery(id+"F19.opExtrude","SWEPT_FACE",FACE,{"disambiguationData":[OSD([sQuery(id+"F18.wireOp",EDGE,"E37.right")])]});
            extrude(context, id + "F23", {"entities" : qUnion([Q0]), "operationType" : NewBodyOperationType.REMOVE, "endBound" : BoundingType.UP_TO_SURFACE, "oppositeDirection" : true, "depth" : 25 * mm, "endBoundEntityFace" : qUnion([Q1]), "offsetDistance" : 25 * mm});
        }
        {
            var Q0;
            Q0=makeQuery(id+"F22.imprint","IMPRINT",FACE,{"disambiguationData":[TD([[makeQuery(id+"F22.imprint","IMPRINT",EDGE,{"derivedFrom":sQuery(id+"F22.wireOp",EDGE,"E43.bottom")}),1.0]])]});
            extrude(context, id + "F24", {"entities" : qUnion([Q0]), "operationType" : NewBodyOperationType.REMOVE, "oppositeDirection" : true, "depth" : 1.5 * mm, "offsetDistance" : 25 * mm});
        }
        {
            var Q0;
            Q0=makeQuery(id+"F17.boolean.opBoolean","COPY",EDGE,{"derivedFrom":makeQuery(id+"F17.opExtrude","CAP_EDGE",EDGE,{"disambiguationData":[OSD([sQuery(id+"F16.wireOp",EDGE,"E36.right")])],"isStart":false})});
            var Q1;
            Q1=makeQuery(id+"F17.boolean.opBoolean","COPY",EDGE,{"derivedFrom":makeQuery(id+"F17.opExtrude","CAP_EDGE",EDGE,{"disambiguationData":[OSD([sQuery(id+"F16.wireOp",EDGE,"E36.top")])],"isStart":false})});
            var Q2;
            Q2=makeQuery(id+"F17.boolean.opBoolean","COPY",EDGE,{"derivedFrom":makeQuery(id+"F17.opExtrude","CAP_EDGE",EDGE,{"disambiguationData":[OSD([sQuery(id+"F16.wireOp",EDGE,"E36.left")])],"isStart":false})});
            var Q3;
            Q3=makeQuery(id+"F24.boolean.opBoolean","COPY",EDGE,{"derivedFrom":makeQuery(id+"F24.opExtrude","CAP_EDGE",EDGE,{"disambiguationData":[OSD([sQuery(id+"F22.wireOp",EDGE,"E43.right")])],"isStart":false})});
            var Q4;
            Q4=makeQuery(id+"F24.boolean.opBoolean","COPY",EDGE,{"derivedFrom":makeQuery(id+"F24.opExtrude","CAP_EDGE",EDGE,{"disambiguationData":[OSD([sQuery(id+"F22.wireOp",EDGE,"E43.top")])],"isStart":false})});
            var Q5;
            Q5=makeQuery(id+"F24.boolean.opBoolean","COPY",EDGE,{"derivedFrom":makeQuery(id+"F24.opExtrude","CAP_EDGE",EDGE,{"disambiguationData":[OSD([sQuery(id+"F22.wireOp",EDGE,"E43.left")])],"isStart":false})});
            chamfer(context, id + "F25", {"entities" : qUnion([Q0, Q1, Q2, Q3, Q4, Q5]), "width" : 0.5 * mm, "tangentPropagation" : true});
        }
        {
            var Q0;
            Q0=qCreatedBy(makeId("Top.planeOp"),FACE);
            var sketch = newSketch(context, id + "F26", { "sketchPlane" : qUnion([Q0])});
            skLineSegment(sketch, "E45.bottom", {"start": v(-16.65, 40.44) * mm, "end": v(16.85, 40.44) * mm});
            skLineSegment(sketch, "E45.top", {"start": v(-16.65, 42.44) * mm, "end": v(16.85, 42.44) * mm});
            skLineSegment(sketch, "E45.left", {"start": v(-16.65, 40.44) * mm, "end": v(-16.65, 42.44) * mm});
            skLineSegment(sketch, "E45.right", {"start": v(16.85, 40.44) * mm, "end": v(16.85, 42.44) * mm});
            skSolve(sketch);
        }
        {
            var Q0;
            Q0 = qSketchRegion(id + "F26", true);
            extrude(context, id + "F27", {"entities" : qUnion([Q0]), "operationType" : NewBodyOperationType.ADD, "oppositeDirection" : true, "depth" : 15.5 * mm, "offsetDistance" : 25 * mm});
        }
        {
            var Q0;
            {var subQ0=sQuery(id+"F0.wireOp",EDGE,"E0.bottom");Q0=makeQuery(id+"F27.boolean.opBoolean","MERGE",FACE,{"derivedFrom":[makeQuery(id+"F2.boolean.opBoolean","MERGE",FACE,{"derivedFrom":[makeQuery(id+"F1.opExtrude","SWEPT_FACE",FACE,{"disambiguationData":[OSD([subQ0])]}),makeQuery(id+"F2.opExtrude","SWEPT_FACE",FACE,{"disambiguationData":[OSD([subQ0])]})]}),makeQuery(id+"F27.opExtrude","SWEPT_FACE",FACE,{"disambiguationData":[OSD([sQuery(id+"F26.wireOp",EDGE,"E45.top")])]})]});}
            var sketch = newSketch(context, id + "F28", { "sketchPlane" : qUnion([Q0])});
            skLineSegment(sketch, "E46.bottom", {"start": v(8.07, -15.5) * mm, "end": v(-8.43, -15.5) * mm});
            skLineSegment(sketch, "E46.top", {"start": v(8.07, -14) * mm, "end": v(-8.43, -14) * mm});
            skLineSegment(sketch, "E46.left", {"start": v(8.07, -15.5) * mm, "end": v(8.07, -14) * mm});
            skLineSegment(sketch, "E46.right", {"start": v(-8.43, -15.5) * mm, "end": v(-8.43, -14) * mm});
            skSolve(sketch);
        }
        {
            var Q0;
            Q0=makeQuery(id+"F28.imprint","IMPRINT",FACE,{"disambiguationData":[TD([[makeQuery(id+"F28.imprint","IMPRINT",EDGE,{"derivedFrom":sQuery(id+"F28.wireOp",EDGE,"E46.bottom")}),-1.0]])]});
            extrude(context, id + "F29", {"entities" : qUnion([Q0]), "operationType" : NewBodyOperationType.REMOVE, "oppositeDirection" : true, "depth" : 1 * mm, "offsetDistance" : 25 * mm});
        }
        {
            var Q0;
            Q0=makeQuery(id+"F1.opExtrude","CAP_FACE",FACE,{"disambiguationData":[OSD([sQuery(id+"F0.wireOp",EDGE,"E0.bottom"),sQuery(id+"F0.wireOp",EDGE,"E0.top"),sQuery(id+"F0.wireOp",EDGE,"E0.left"),sQuery(id+"F0.wireOp",EDGE,"E0.right"),sQuery(id+"F0.wireOp",EDGE,"E7"),sQuery(id+"F0.wireOp",EDGE,"E8"),sQuery(id+"F0.wireOp",EDGE,"E9"),sQuery(id+"F0.wireOp",EDGE,"E10"),sQuery(id+"F0.wireOp",EDGE,"E11.MirrorCS"),sQuery(id+"F0.wireOp",EDGE,"E12.MirrorCS"),sQuery(id+"F0.wireOp",EDGE,"E13.MirrorCS"),sQuery(id+"F0.wireOp",EDGE,"E14.MirrorC"),sQuery(id+"F0.wireOp",EDGE,"E15"),sQuery(id+"F0.wireOp",EDGE,"E16"),sQuery(id+"F0.wireOp",EDGE,"E17"),sQuery(id+"F0.wireOp",EDGE,"E18"),sQuery(id+"F0.wireOp",EDGE,"E19.trimOffspring"),sQuery(id+"F0.wireOp",EDGE,"E20.MirrorC"),sQuery(id+"F0.wireOp",EDGE,"E21.MirrorCS"),sQuery(id+"F0.wireOp",EDGE,"E22.MirrorCS"),sQuery(id+"F0.wireOp",EDGE,"E23.MirrorCS"),sQuery(id+"F0.wireOp",EDGE,"E24.trimOffspring")])],"isStart":true});
            var sketch = newSketch(context, id + "F30", { "sketchPlane" : qUnion([Q0])});
            skCircle(sketch, "E47", {"center": v(0, 14.44) * mm, "radius": 19 * mm});
            skCircle(sketch, "E48", {"center": v(-16.5, 30.94) * mm, "radius": 1.5 * mm});
            skCircle(sketch, "E49", {"center": v(-16.5, -2.06) * mm, "radius": 1.5 * mm});
            skCircle(sketch, "E50", {"center": v(16.5, 30.94) * mm, "radius": 1.5 * mm});
            skCircle(sketch, "E51", {"center": v(16.5, -2.06) * mm, "radius": 1.5 * mm});
            skSolve(sketch);
        }
        {
            var Q0;
            Q0 = qSketchRegion(id + "F30", true);
            var Q1;
            Q1=makeQuery(id+"F1.opExtrude","CAP_FACE",FACE,{"disambiguationData":[OSD([sQuery(id+"F0.wireOp",EDGE,"E0.bottom"),sQuery(id+"F0.wireOp",EDGE,"E0.top"),sQuery(id+"F0.wireOp",EDGE,"E0.left"),sQuery(id+"F0.wireOp",EDGE,"E0.right"),sQuery(id+"F0.wireOp",EDGE,"E7"),sQuery(id+"F0.wireOp",EDGE,"E8"),sQuery(id+"F0.wireOp",EDGE,"E9"),sQuery(id+"F0.wireOp",EDGE,"E10"),sQuery(id+"F0.wireOp",EDGE,"E11.MirrorCS"),sQuery(id+"F0.wireOp",EDGE,"E12.MirrorCS"),sQuery(id+"F0.wireOp",EDGE,"E13.MirrorCS"),sQuery(id+"F0.wireOp",EDGE,"E14.MirrorC"),sQuery(id+"F0.wireOp",EDGE,"E15"),sQuery(id+"F0.wireOp",EDGE,"E16"),sQuery(id+"F0.wireOp",EDGE,"E17"),sQuery(id+"F0.wireOp",EDGE,"E18"),sQuery(id+"F0.wireOp",EDGE,"E19.trimOffspring"),sQuery(id+"F0.wireOp",EDGE,"E20.MirrorC"),sQuery(id+"F0.wireOp",EDGE,"E21.MirrorCS"),sQuery(id+"F0.wireOp",EDGE,"E22.MirrorCS"),sQuery(id+"F0.wireOp",EDGE,"E23.MirrorCS"),sQuery(id+"F0.wireOp",EDGE,"E24.trimOffspring")])],"isStart":false});
            extrude(context, id + "F31", {"entities" : qUnion([Q0]), "operationType" : NewBodyOperationType.REMOVE, "endBound" : BoundingType.UP_TO_SURFACE, "oppositeDirection" : true, "depth" : 25 * mm, "endBoundEntityFace" : qUnion([Q1]), "offsetDistance" : 25 * mm});
        }
        {
            var Q0;
            Q0=makeQuery(id+"F1.opExtrude","CAP_FACE",FACE,{"disambiguationData":[OSD([sQuery(id+"F0.wireOp",EDGE,"E0.bottom"),sQuery(id+"F0.wireOp",EDGE,"E0.top"),sQuery(id+"F0.wireOp",EDGE,"E0.left"),sQuery(id+"F0.wireOp",EDGE,"E0.right"),sQuery(id+"F0.wireOp",EDGE,"E7"),sQuery(id+"F0.wireOp",EDGE,"E8"),sQuery(id+"F0.wireOp",EDGE,"E9"),sQuery(id+"F0.wireOp",EDGE,"E10"),sQuery(id+"F0.wireOp",EDGE,"E11.MirrorCS"),sQuery(id+"F0.wireOp",EDGE,"E12.MirrorCS"),sQuery(id+"F0.wireOp",EDGE,"E13.MirrorCS"),sQuery(id+"F0.wireOp",EDGE,"E14.MirrorC"),sQuery(id+"F0.wireOp",EDGE,"E15"),sQuery(id+"F0.wireOp",EDGE,"E16"),sQuery(id+"F0.wireOp",EDGE,"E17"),sQuery(id+"F0.wireOp",EDGE,"E18"),sQuery(id+"F0.wireOp",EDGE,"E19.trimOffspring"),sQuery(id+"F0.wireOp",EDGE,"E20.MirrorC"),sQuery(id+"F0.wireOp",EDGE,"E21.MirrorCS"),sQuery(id+"F0.wireOp",EDGE,"E22.MirrorCS"),sQuery(id+"F0.wireOp",EDGE,"E23.MirrorCS"),sQuery(id+"F0.wireOp",EDGE,"E24.trimOffspring")])],"isStart":true});
            var sketch = newSketch(context, id + "F32", { "sketchPlane" : qUnion([Q0])});
            skLineSegment(sketch, "E52.bottom", {"start": v(22.49, 32.1) * mm, "end": v(26.49, 32.1) * mm});
            skLineSegment(sketch, "E52.top", {"start": v(22.49, 8.24) * mm, "end": v(26.49, 8.24) * mm});
            skLineSegment(sketch, "E52.left", {"start": v(22.49, 32.1) * mm, "end": v(22.49, 8.24) * mm});
            skLineSegment(sketch, "E52.right", {"start": v(26.49, 32.1) * mm, "end": v(26.49, 8.24) * mm});
            skLineSegment(sketch, "E53.bottom", {"start": v(22.49, 5.24) * mm, "end": v(26.49, 5.24) * mm});
            skLineSegment(sketch, "E53.top", {"start": v(22.49, -18.6) * mm, "end": v(26.49, -18.6) * mm});
            skLineSegment(sketch, "E53.left", {"start": v(22.49, 5.24) * mm, "end": v(22.49, -18.6) * mm});
            skLineSegment(sketch, "E53.right", {"start": v(26.49, 5.24) * mm, "end": v(26.49, -18.6) * mm});
            skLineSegment(sketch, "E54.0", {"start": v(21.49, 33.1) * mm, "end": v(27.49, 33.1) * mm});
            skLineSegment(sketch, "E54.1", {"start": v(21.49, 33.1) * mm, "end": v(21.49, 7.24) * mm});
            skLineSegment(sketch, "E54.2", {"start": v(21.49, 7.24) * mm, "end": v(27.49, 7.24) * mm});
            skLineSegment(sketch, "E54.3", {"start": v(27.49, 33.1) * mm, "end": v(27.49, 7.24) * mm});
            skLineSegment(sketch, "E55.0", {"start": v(21.49, 6.24) * mm, "end": v(27.49, 6.24) * mm});
            skLineSegment(sketch, "E55.1", {"start": v(21.49, 6.24) * mm, "end": v(21.49, -19.6) * mm});
            skLineSegment(sketch, "E55.2", {"start": v(21.49, -19.6) * mm, "end": v(27.49, -19.6) * mm});
            skLineSegment(sketch, "E55.3", {"start": v(27.49, 6.24) * mm, "end": v(27.49, -19.6) * mm});
            skLineSegment(sketch, "E56", {"start": v(23.99, 33.1) * mm, "end": v(23.99, 32.1) * mm});
            skLineSegment(sketch, "E57", {"start": v(24.99, 33.1) * mm, "end": v(24.99, 32.1) * mm});
            skLineSegment(sketch, "E58", {"start": v(23.99, 8.24) * mm, "end": v(23.99, 7.24) * mm});
            skLineSegment(sketch, "E59", {"start": v(24.99, 8.24) * mm, "end": v(24.99, 7.24) * mm});
            skLineSegment(sketch, "E60", {"start": v(23.99, 6.24) * mm, "end": v(23.99, 5.24) * mm});
            skLineSegment(sketch, "E61", {"start": v(24.99, 6.24) * mm, "end": v(24.99, 5.24) * mm});
            skLineSegment(sketch, "E62", {"start": v(23.99, -18.6) * mm, "end": v(23.99, -19.6) * mm});
            skLineSegment(sketch, "E63", {"start": v(24.99, -18.6) * mm, "end": v(24.99, -19.6) * mm});
            skLineSegment(sketch, "E64", {"start": v(21.49, 0.24) * mm, "end": v(22.49, 0.24) * mm});
            skLineSegment(sketch, "E65", {"start": v(21.49, -0.76) * mm, "end": v(22.49, -0.76) * mm});
            skLineSegment(sketch, "E66", {"start": v(26.49, 0.24) * mm, "end": v(27.49, 0.24) * mm});
            skLineSegment(sketch, "E67", {"start": v(26.49, -0.76) * mm, "end": v(27.49, -0.76) * mm});
            skLineSegment(sketch, "E68", {"start": v(21.49, -12.76) * mm, "end": v(22.49, -12.76) * mm});
            skLineSegment(sketch, "E69", {"start": v(21.49, -13.76) * mm, "end": v(22.49, -13.76) * mm});
            skLineSegment(sketch, "E70", {"start": v(26.49, -12.76) * mm, "end": v(27.49, -12.76) * mm});
            skLineSegment(sketch, "E71", {"start": v(26.49, -13.76) * mm, "end": v(27.49, -13.76) * mm});
            skLineSegment(sketch, "E72", {"start": v(21.49, 27.1) * mm, "end": v(22.49, 27.1) * mm});
            skLineSegment(sketch, "E73", {"start": v(21.49, 26.1) * mm, "end": v(22.49, 26.1) * mm});
            skLineSegment(sketch, "E74", {"start": v(26.49, 27.1) * mm, "end": v(27.49, 27.1) * mm});
            skLineSegment(sketch, "E75", {"start": v(26.49, 26.1) * mm, "end": v(27.49, 26.1) * mm});
            skLineSegment(sketch, "E76", {"start": v(21.49, 14.1) * mm, "end": v(22.49, 14.1) * mm});
            skLineSegment(sketch, "E77", {"start": v(21.49, 13.1) * mm, "end": v(22.49, 13.1) * mm});
            skLineSegment(sketch, "E78", {"start": v(26.49, 14.1) * mm, "end": v(27.49, 14.1) * mm});
            skLineSegment(sketch, "E79", {"start": v(26.49, 13.1) * mm, "end": v(27.49, 13.1) * mm});
            skLineSegment(sketch, "E80.bottom", {"start": v(-9, 36.8) * mm, "end": v(9, 36.8) * mm});
            skLineSegment(sketch, "E80.top", {"start": v(-9, 34) * mm, "end": v(9, 34) * mm});
            skLineSegment(sketch, "E80.left", {"start": v(-9, 36.8) * mm, "end": v(-9, 34) * mm});
            skLineSegment(sketch, "E80.right", {"start": v(9, 36.8) * mm, "end": v(9, 34) * mm});
            skPoint(sketch, "E80.middle", {"position": v(0, 35.4) * mm});
            skLineSegment(sketch, "E81.bottom", {"start": v(-7.5, -4.3) * mm, "end": v(-25.5, -4.3) * mm});
            skLineSegment(sketch, "E81.top", {"start": v(-7.5, -7.1) * mm, "end": v(-25.5, -7.1) * mm});
            skLineSegment(sketch, "E81.left", {"start": v(-7.5, -4.3) * mm, "end": v(-7.5, -7.1) * mm});
            skLineSegment(sketch, "E81.right", {"start": v(-25.5, -4.3) * mm, "end": v(-25.5, -7.1) * mm});
            skPoint(sketch, "E81.middle", {"position": v(-16.5, -5.7) * mm});
            skSolve(sketch);
        }
        {
            var Q0;
            {var subQ3=sQuery(id+"F32.wireOp",EDGE,"E56");Q0=makeQuery(id+"F32.imprint","IMPRINT",FACE,{"disambiguationData":[TD([[makeQuery(id+"F32.imprint","IMPRINT",EDGE,{"derivedFrom":subQ3}),-1.0]])]});}
            var Q1;
            {var subQ4=sQuery(id+"F32.wireOp",EDGE,"E57");Q1=makeQuery(id+"F32.imprint","IMPRINT",FACE,{"disambiguationData":[TD([[makeQuery(id+"F32.imprint","IMPRINT",EDGE,{"derivedFrom":subQ4}),1.0]])]});}
            var Q2;
            {var subQ0=sQuery(id+"F32.wireOp",EDGE,"E73");Q2=makeQuery(id+"F32.imprint","IMPRINT",FACE,{"disambiguationData":[TD([[makeQuery(id+"F32.imprint","IMPRINT",EDGE,{"derivedFrom":subQ0}),-1.0]])]});}
            var Q3;
            {var subQ0=sQuery(id+"F32.wireOp",EDGE,"E75");Q3=makeQuery(id+"F32.imprint","IMPRINT",FACE,{"disambiguationData":[TD([[makeQuery(id+"F32.imprint","IMPRINT",EDGE,{"derivedFrom":subQ0}),-1.0]])]});}
            var Q4;
            {var subQ4=sQuery(id+"F32.wireOp",EDGE,"E58");Q4=makeQuery(id+"F32.imprint","IMPRINT",FACE,{"disambiguationData":[TD([[makeQuery(id+"F32.imprint","IMPRINT",EDGE,{"derivedFrom":subQ4}),-1.0]])]});}
            var Q5;
            {var subQ4=sQuery(id+"F32.wireOp",EDGE,"E59");Q5=makeQuery(id+"F32.imprint","IMPRINT",FACE,{"disambiguationData":[TD([[makeQuery(id+"F32.imprint","IMPRINT",EDGE,{"derivedFrom":subQ4}),1.0]])]});}
            var Q6;
            {var subQ3=sQuery(id+"F32.wireOp",EDGE,"E60");Q6=makeQuery(id+"F32.imprint","IMPRINT",FACE,{"disambiguationData":[TD([[makeQuery(id+"F32.imprint","IMPRINT",EDGE,{"derivedFrom":subQ3}),-1.0]])]});}
            var Q7;
            {var subQ4=sQuery(id+"F32.wireOp",EDGE,"E61");Q7=makeQuery(id+"F32.imprint","IMPRINT",FACE,{"disambiguationData":[TD([[makeQuery(id+"F32.imprint","IMPRINT",EDGE,{"derivedFrom":subQ4}),1.0]])]});}
            var Q8;
            {var subQ0=sQuery(id+"F32.wireOp",EDGE,"E65");Q8=makeQuery(id+"F32.imprint","IMPRINT",FACE,{"disambiguationData":[TD([[makeQuery(id+"F32.imprint","IMPRINT",EDGE,{"derivedFrom":subQ0}),-1.0]])]});}
            var Q9;
            {var subQ0=sQuery(id+"F32.wireOp",EDGE,"E67");Q9=makeQuery(id+"F32.imprint","IMPRINT",FACE,{"disambiguationData":[TD([[makeQuery(id+"F32.imprint","IMPRINT",EDGE,{"derivedFrom":subQ0}),-1.0]])]});}
            var Q10;
            {var subQ4=sQuery(id+"F32.wireOp",EDGE,"E62");Q10=makeQuery(id+"F32.imprint","IMPRINT",FACE,{"disambiguationData":[TD([[makeQuery(id+"F32.imprint","IMPRINT",EDGE,{"derivedFrom":subQ4}),-1.0]])]});}
            var Q11;
            {var subQ4=sQuery(id+"F32.wireOp",EDGE,"E63");Q11=makeQuery(id+"F32.imprint","IMPRINT",FACE,{"disambiguationData":[TD([[makeQuery(id+"F32.imprint","IMPRINT",EDGE,{"derivedFrom":subQ4}),1.0]])]});}
            var Q12;
            Q12=makeQuery(id+"F32.imprint","IMPRINT",FACE,{"disambiguationData":[TD([[makeQuery(id+"F32.imprint","IMPRINT",EDGE,{"derivedFrom":sQuery(id+"F32.wireOp",EDGE,"E81.bottom")}),1.0]])]});
            var Q13;
            Q13=makeQuery(id+"F32.imprint","IMPRINT",FACE,{"disambiguationData":[TD([[makeQuery(id+"F32.imprint","IMPRINT",EDGE,{"derivedFrom":sQuery(id+"F32.wireOp",EDGE,"E80.bottom")}),-1.0]])]});
            var Q14;
            Q14=makeQuery(id+"F1.opExtrude","CAP_FACE",FACE,{"disambiguationData":[OSD([sQuery(id+"F0.wireOp",EDGE,"E0.bottom"),sQuery(id+"F0.wireOp",EDGE,"E0.top"),sQuery(id+"F0.wireOp",EDGE,"E0.left"),sQuery(id+"F0.wireOp",EDGE,"E0.right"),sQuery(id+"F0.wireOp",EDGE,"E7"),sQuery(id+"F0.wireOp",EDGE,"E8"),sQuery(id+"F0.wireOp",EDGE,"E9"),sQuery(id+"F0.wireOp",EDGE,"E10"),sQuery(id+"F0.wireOp",EDGE,"E11.MirrorCS"),sQuery(id+"F0.wireOp",EDGE,"E12.MirrorCS"),sQuery(id+"F0.wireOp",EDGE,"E13.MirrorCS"),sQuery(id+"F0.wireOp",EDGE,"E14.MirrorC"),sQuery(id+"F0.wireOp",EDGE,"E15"),sQuery(id+"F0.wireOp",EDGE,"E16"),sQuery(id+"F0.wireOp",EDGE,"E17"),sQuery(id+"F0.wireOp",EDGE,"E18"),sQuery(id+"F0.wireOp",EDGE,"E19.trimOffspring"),sQuery(id+"F0.wireOp",EDGE,"E20.MirrorC"),sQuery(id+"F0.wireOp",EDGE,"E21.MirrorCS"),sQuery(id+"F0.wireOp",EDGE,"E22.MirrorCS"),sQuery(id+"F0.wireOp",EDGE,"E23.MirrorCS"),sQuery(id+"F0.wireOp",EDGE,"E24.trimOffspring")])],"isStart":false});
            extrude(context, id + "F33", {"entities" : qUnion([Q0, Q1, Q2, Q3, Q4, Q5, Q6, Q7, Q8, Q9, Q10, Q11, Q12, Q13]), "operationType" : NewBodyOperationType.REMOVE, "endBound" : BoundingType.UP_TO_SURFACE, "oppositeDirection" : true, "depth" : 25 * mm, "endBoundEntityFace" : qUnion([Q14]), "offsetDistance" : 25 * mm});
        }
        {
            var Q0;
            Q0=makeQuery(id+"F33.boolean.opBoolean","COPY",EDGE,{"derivedFrom":makeQuery(id+"F33.opExtrude","SWEPT_EDGE",EDGE,{"disambiguationData":[OSD([sQuery(id+"F32.wireOp",EDGE,"E81.bottom"),sQuery(id+"F32.wireOp",EDGE,"E81.right")])]})});
            var Q1;
            Q1=makeQuery(id+"F33.boolean.opBoolean","COPY",EDGE,{"derivedFrom":makeQuery(id+"F33.opExtrude","SWEPT_EDGE",EDGE,{"disambiguationData":[OSD([sQuery(id+"F32.wireOp",EDGE,"E81.top"),sQuery(id+"F32.wireOp",EDGE,"E81.right")])]})});
            var Q2;
            Q2=makeQuery(id+"F33.boolean.opBoolean","COPY",EDGE,{"derivedFrom":makeQuery(id+"F33.opExtrude","SWEPT_EDGE",EDGE,{"disambiguationData":[OSD([sQuery(id+"F32.wireOp",EDGE,"E81.top"),sQuery(id+"F32.wireOp",EDGE,"E81.left")])]})});
            var Q3;
            Q3=makeQuery(id+"F33.boolean.opBoolean","COPY",EDGE,{"derivedFrom":makeQuery(id+"F33.opExtrude","SWEPT_EDGE",EDGE,{"disambiguationData":[OSD([sQuery(id+"F32.wireOp",EDGE,"E81.bottom"),sQuery(id+"F32.wireOp",EDGE,"E81.left")])]})});
            var Q4;
            Q4=makeQuery(id+"F33.boolean.opBoolean","COPY",EDGE,{"derivedFrom":makeQuery(id+"F33.opExtrude","SWEPT_EDGE",EDGE,{"disambiguationData":[OSD([sQuery(id+"F32.wireOp",EDGE,"E80.bottom"),sQuery(id+"F32.wireOp",EDGE,"E80.right")])]})});
            var Q5;
            Q5=makeQuery(id+"F33.boolean.opBoolean","COPY",EDGE,{"derivedFrom":makeQuery(id+"F33.opExtrude","SWEPT_EDGE",EDGE,{"disambiguationData":[OSD([sQuery(id+"F32.wireOp",EDGE,"E80.bottom"),sQuery(id+"F32.wireOp",EDGE,"E80.left")])]})});
            var Q6;
            Q6=makeQuery(id+"F33.boolean.opBoolean","COPY",EDGE,{"derivedFrom":makeQuery(id+"F33.opExtrude","SWEPT_EDGE",EDGE,{"disambiguationData":[OSD([sQuery(id+"F32.wireOp",EDGE,"E80.top"),sQuery(id+"F32.wireOp",EDGE,"E80.left")])]})});
            var Q7;
            Q7=makeQuery(id+"F33.boolean.opBoolean","COPY",EDGE,{"derivedFrom":makeQuery(id+"F33.opExtrude","SWEPT_EDGE",EDGE,{"disambiguationData":[OSD([sQuery(id+"F32.wireOp",EDGE,"E80.top"),sQuery(id+"F32.wireOp",EDGE,"E80.right")])]})});
            fillet(context, id + "F34", {"entities" : qUnion([Q0, Q1, Q2, Q3, Q4, Q5, Q6, Q7]), "radius" : 0.5 * mm, "tangentPropagation" : true, "allowEdgeOverflow" : false});
        }
    });
